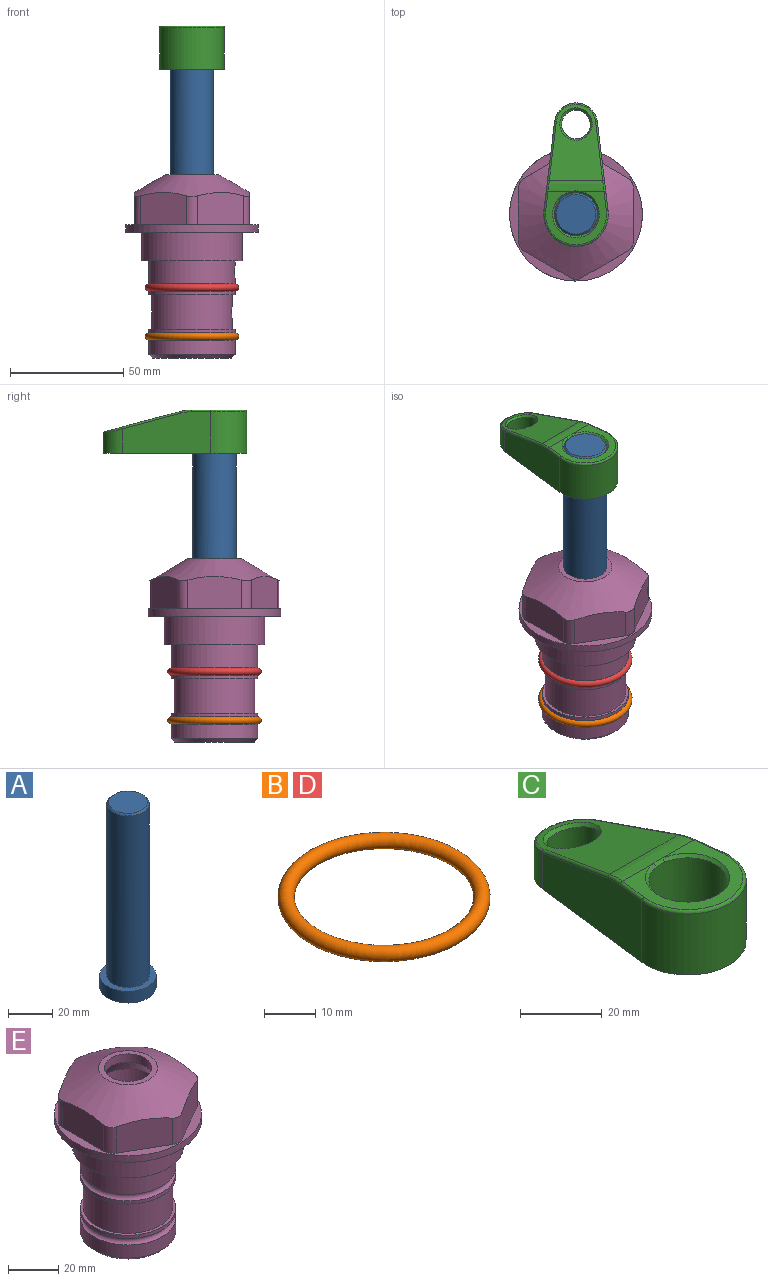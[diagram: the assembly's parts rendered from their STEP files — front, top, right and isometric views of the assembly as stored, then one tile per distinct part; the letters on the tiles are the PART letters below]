
ASSEMBLY  parts=5 mates=4
PART A: 6 faces, bbox 25.4x25.4x101.6 mm
  f0: plane 17.46x17.46mm, normal (0,0,1), area 239.5mm2, adj f5
  f1: plane 25.4x25.4mm, normal (0,0,-1), area 506.7mm2, adj f2
  f2: cylinder r=12.7mm len=25.4mm, axis (0,0,1), area 506.7mm2, adj f1,f3
  f3: plane 25.4x25.4mm, normal (0,0,1), area 221.7mm2, adj f2,f4
  f4: cylinder r=9.53mm len=94.46mm, axis (0,0,1), area 5653mm2, adj f3,f5
  f5: cone r=8.73mm half-angle=45deg, axis (0,0,-1), area 64.4mm2, adj f0,f4
PART B: 1 faces, bbox 44.7x44.7x3.2 mm
  f0: torus R=19.05mm, axis (0,0,1), area 1193.9mm2
PART C: 31 faces, bbox 31.7x65.5x19.8 mm
  f0: plane 39.12x18.26mm, normal (0.99,0.12,0), area 612.2mm2, adj f1,f4,f7,f11,f13,f15
  f1: cylinder r=9.53mm len=18.91mm, axis (0,0,-1), area 296.1mm2, adj f0,f2,f7,f17
  f2: plane 39.12x18.26mm, normal (-0.99,0.12,0), area 612.2mm2, adj f1,f4,f7,f12,f14,f16
  f3: cylinder r=6.35mm len=12.7mm, axis (0,0,-1), area 362.4mm2, adj f7,f18
  f4: cylinder r=14.29mm len=28.58mm, axis (0,0,-1), area 882.2mm2, adj f0,f2,f7,f10
  f5: cylinder r=9.53mm len=19.05mm, axis (0,0,-1), area 1092.6mm2, adj f7,f19,f20
  f6: plane 26.99x23.69mm, normal (0,0,1), area 216.2mm2, adj f9,f10,f11,f12,f19
  f7: plane 63.5x28.58mm, normal (0,0,-1), area 661.8mm2, adj f0,f1,f2,f3,f4,f5,f22,f23
  f8: plane 33.52x23.6mm, normal (0,0.26,0.97), area 486mm2, adj f9,f15,f16,f17,f18
  f9: cylinder r=19.05mm len=24.72mm, axis (1,0,0), area 120.4mm2, adj f6,f8,f13,f14,f20
  f10: torus R=13.49mm, axis (0,0,1), area 59mm2, adj f4,f6,f11,f12
  f11: cylinder r=0.79mm len=8.67mm, axis (0.12,-0.99,0), area 10.8mm2, adj f0,f6,f10,f13
  f12: cylinder r=0.79mm len=8.67mm, axis (0.12,0.99,0), area 10.8mm2, adj f2,f6,f10,f14
  f13: bspline ~4.95x1.42mm, area 6.1mm2, adj f0,f9,f11,f15
  f14: bspline ~4.95x1.42mm, area 6.1mm2, adj f2,f9,f12,f16
  f15: cylinder r=0.79mm len=25.95mm, axis (0.12,-0.96,0.26), area 32.9mm2, adj f0,f8,f13,f17
  f16: cylinder r=0.79mm len=25.95mm, axis (0.12,0.96,-0.26), area 32.9mm2, adj f2,f8,f14,f17
  f17: bspline ~18.91x8.38mm, area 30mm2, adj f1,f8,f15,f16
  f18: bspline ~14.29x14.29mm, area 48.3mm2, adj f3,f8
  f19: cone r=9.53mm half-angle=45deg, axis (0,0,1), area 66.5mm2, adj f5,f6,f20
  f20: bspline ~3.22x0.96mm, area 3.5mm2, adj f5,f9,f19
  f21: plane 2.75x2.72mm, normal (0,0,-1), area 2.9mm2, adj f23,f25,f28
  f22: plane 23.05x15.88mm, normal (-0.99,-0.12,0), area 323.6mm2, adj f7,f25,f26,f27,f28,f29
  f23: plane 23.05x15.88mm, normal (0.99,-0.12,0), area 323.6mm2, adj f7,f21,f25,f27,f28,f30
  f24: cylinder r=9.53mm len=10.69mm, axis (0,0,-1), area 114.7mm2, adj f7,f27,f29,f30
  f25: cylinder r=12.7mm len=20.59mm, axis (0,0,-1), area 381.1mm2, adj f7,f21,f22,f23,f26,f28
  f26: plane 2.75x2.72mm, normal (0,0,-1), area 2.9mm2, adj f22,f25,f28
  f27: plane 19.72x18.37mm, normal (0,-0.26,-0.97), area 291.8mm2, adj f22,f23,f24,f28,f29,f30
  f28: cylinder r=15.88mm len=19.92mm, axis (1,0,0), area 54.8mm2, adj f21,f22,f23,f25,f26,f27
  f29: cylinder r=1.59mm len=11mm, axis (0,0,-1), area 34.7mm2, adj f7,f22,f24,f27
  f30: cylinder r=1.59mm len=11mm, axis (0,0,-1), area 34.7mm2, adj f7,f23,f24,f27
PART D: same geometry as B
PART E: 36 faces, bbox 58.7x58.7x81 mm
  f0: cylinder r=17.78mm len=35.56mm, axis (0,0,1), area 1670.8mm2, adj f23,f24,f31
  f1: cylinder r=19.05mm len=38.1mm, axis (0,0,1), area 1191.9mm2, adj f26,f27,f30
  f2: plane 58.66x58.66mm, normal (0,0,-1), area 1150.6mm2, adj f3,f28
  f3: cylinder r=29.33mm len=58.66mm, axis (0,0,-1), area 585.1mm2, adj f2,f4
  f4: plane 58.66x58.66mm, normal (0,0,1), area 475.9mm2, adj f3,f5,f6,f7,f8,f9,f10,f11
  f5: plane 20.32x14.34mm, normal (-0.5,0.87,0), area 324.4mm2, adj f4,f15,f16,f17
  f6: plane 20.32x14.34mm, normal (0.5,0.87,0), area 324.4mm2, adj f4,f14,f15,f17
  f7: plane 23.48x14.34mm, normal (1,0,0), area 324.4mm2, adj f4,f13,f14,f17
  f8: plane 20.32x14.34mm, normal (0.5,-0.87,0), area 324.4mm2, adj f4,f12,f13,f17
  f9: plane 20.32x14.34mm, normal (-0.5,-0.87,0), area 324.4mm2, adj f4,f11,f12,f17
  f10: plane 23.48x14.34mm, normal (-1,0,0), area 324.4mm2, adj f4,f11,f16,f17
  f11: cylinder r=5.08mm len=12.85mm, axis (0,0,-1), area 67.2mm2, adj f4,f9,f10,f17
  f12: cylinder r=5.08mm len=12.85mm, axis (0,0,-1), area 67.2mm2, adj f4,f8,f9,f17
  f13: cylinder r=5.08mm len=12.85mm, axis (0,0,-1), area 67.2mm2, adj f4,f7,f8,f17
  f14: cylinder r=5.08mm len=12.85mm, axis (0,0,-1), area 67.2mm2, adj f4,f6,f7,f17
  f15: cylinder r=5.08mm len=12.85mm, axis (0,0,-1), area 67.2mm2, adj f4,f5,f6,f17
  f16: cylinder r=5.08mm len=12.85mm, axis (0,0,-1), area 67.2mm2, adj f4,f5,f10,f17
  f17: cone r=11.73mm half-angle=60deg, axis (0,0,-1), area 2071.8mm2, adj f5,f6,f7,f8,f9,f10,f11,f12
  f18: plane 23.46x23.46mm, normal (0,0,1), area 147.4mm2, adj f17,f35
  f19: plane 34.93x34.93mm, normal (0,0,-1), area 958mm2, adj f29
  f20: cylinder r=19.05mm len=38.1mm, axis (0,0,1), area 760.1mm2, adj f21,f29
  f21: torus R=19.05mm, axis (0,0,1), area 565.3mm2, adj f20,f22
  f22: cylinder r=19.05mm len=38.1mm, axis (0,0,1), area 190mm2, adj f21,f23
  f23: plane 38.1x38.1mm, normal (0,0,1), area 146.9mm2, adj f0,f22
  f24: plane 38.1x38.1mm, normal (0,0,-1), area 146.9mm2, adj f0,f25
  f25: cylinder r=19.05mm len=38.1mm, axis (0,0,1), area 190mm2, adj f24,f26
  f26: torus R=19.05mm, axis (0,0,1), area 565.3mm2, adj f1,f25
  f27: plane 44.45x44.45mm, normal (0,0,-1), area 411.7mm2, adj f1,f28
  f28: cylinder r=22.23mm len=44.45mm, axis (0,0,1), area 1773.5mm2, adj f2,f27
  f29: cone r=19.05mm half-angle=45deg, axis (0,0,1), area 257.5mm2, adj f19,f20
  f30: cylinder r=3.17mm len=6.75mm, axis (-1,0,0), area 128mm2, adj f1,f33
  f31: cylinder r=3.17mm len=6.35mm, axis (-1,0,0), area 102.5mm2, adj f0,f33
  f32: plane 25.4x25.4mm, normal (0,0,1), area 506.7mm2, adj f33
  f33: cylinder r=12.7mm len=66.42mm, axis (0,0,-1), area 5236.2mm2, adj f30,f31,f32,f34
  f34: cone r=9.53mm half-angle=30deg, axis (0,0,-1), area 443.4mm2, adj f33,f35
  f35: cylinder r=9.53mm len=19.05mm, axis (0,0,-1), area 240.9mm2, adj f18,f34
PLACE A t=(0,0,27.55)mm
PLACE B t=(0,0,-21.59)mm
PLACE C t=(0,0,27.55)mm
PLACE D at identity
PLACE E at identity fixed
MATE fastened A.f2 <-> C.f4  axis (0,0,1) through (0,0,91.05)mm
MATE fastened B.f0 <-> E.f0  axis (0,0,1) through (0,0,-46.1)mm
MATE fastened D.f0 <-> E.f0  axis (0,0,1) through (0,0,-24.51)mm
MATE cylindrical A.f2 <-> E.f0  axis (0,0,-1) through (0,0,-10.55)mm
